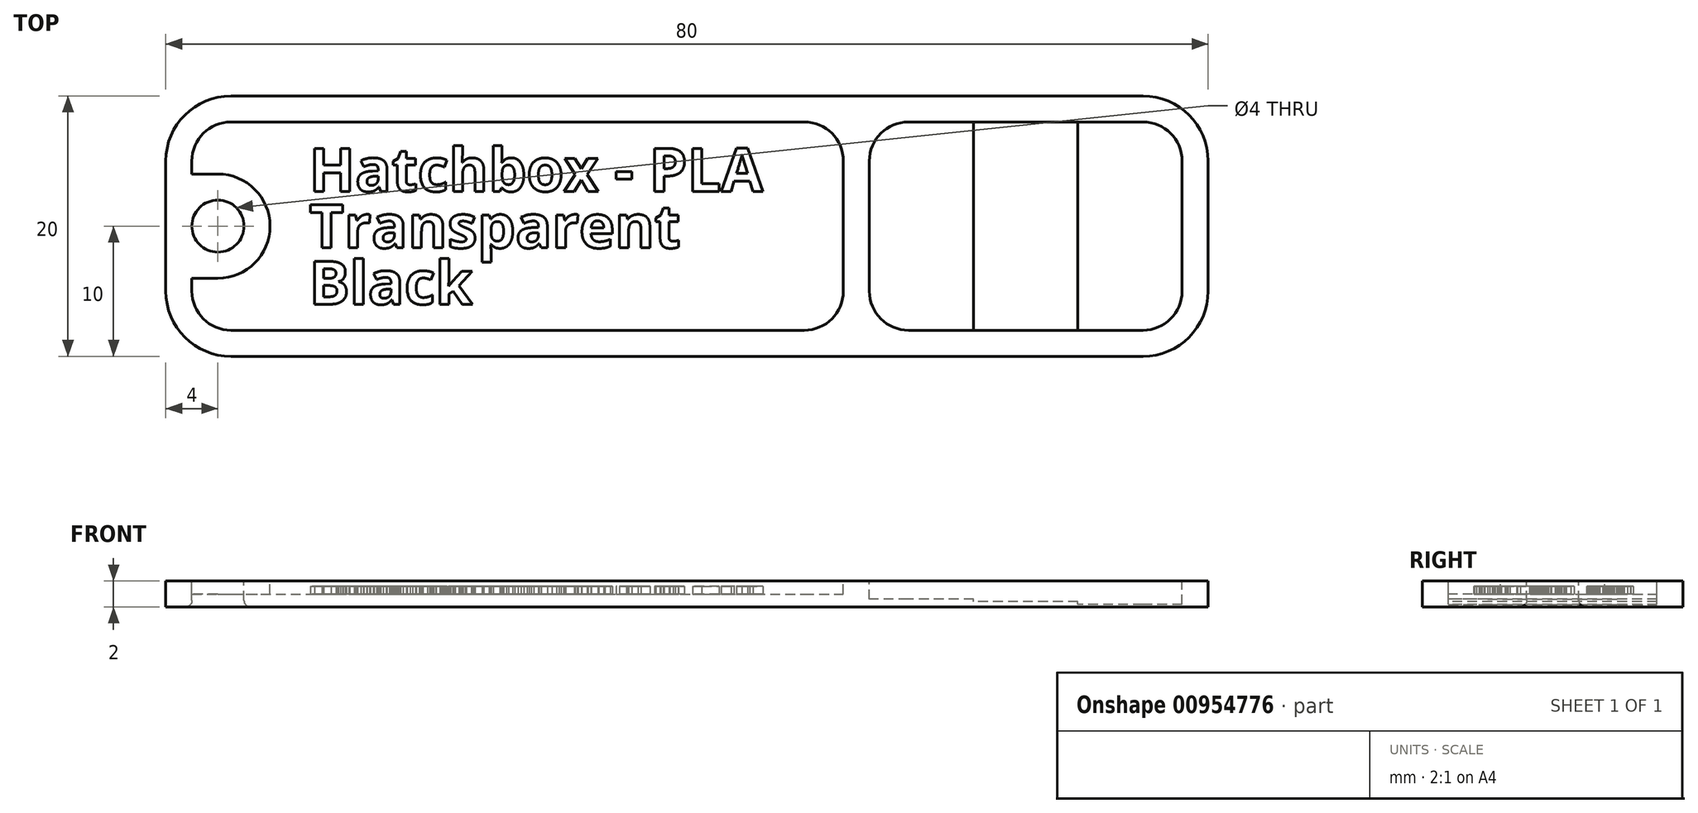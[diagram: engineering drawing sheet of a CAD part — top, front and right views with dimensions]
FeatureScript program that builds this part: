
annotation { "Feature Type Name" : "Feature", "Feature Type Description" : "" }
export const myFeature = defineFeature(function(context is Context, id is Id, definition is map)
    precondition{}
    {
        {
            var Q0;
            Q0=qCreatedBy(makeId("Top.planeOp"),FACE);
            var sketch = newSketch(context, id + "F0", { "sketchPlane" : qUnion([Q0])});
            skLineSegment(sketch, "E0.bottom", {"start": v(35, 10) * mm, "end": v(-35, 10) * mm});
            skLineSegment(sketch, "E0.top", {"start": v(35, -10) * mm, "end": v(-35, -10) * mm});
            skLineSegment(sketch, "E0.left", {"start": v(40, 5) * mm, "end": v(40, -5) * mm});
            skLineSegment(sketch, "E0.right", {"start": v(-40, 5) * mm, "end": v(-40, -5) * mm});
            skPoint(sketch, "E0.middle", {"position": v(0, 0) * mm});
            skPoint(sketch, "E1.visualSharp", {"position": v(-40, 10) * mm});
            skArc(sketch, "E1.filletArc", {"start": v(-35, 10) * mm, "mid": v(-38.54, 8.54) * mm, "end": v(-40, 5) * mm});
            skPoint(sketch, "E2.visualSharp", {"position": v(40, 10) * mm});
            skArc(sketch, "E2.filletArc", {"start": v(40, 5) * mm, "mid": v(38.54, 8.54) * mm, "end": v(35, 10) * mm});
            skPoint(sketch, "E3.visualSharp", {"position": v(40, -10) * mm});
            skArc(sketch, "E3.filletArc", {"start": v(35, -10) * mm, "mid": v(38.54, -8.54) * mm, "end": v(40, -5) * mm});
            skPoint(sketch, "E4.visualSharp", {"position": v(-40, -10) * mm});
            skArc(sketch, "E4.filletArc", {"start": v(-40, -5) * mm, "mid": v(-38.54, -8.54) * mm, "end": v(-35, -10) * mm});
            skSolve(sketch);
        }
        {
            var Q0;
            Q0=qSketchRegion(id+"F0",true);
            extrude(context, id + "F1", {"entities" : qUnion([Q0]), "offsetDistance" : 25 * mm, "depth" : 2 * mm});
        }
        {
            var Q0;
            Q0=makeQuery(id+"F1.opExtrude","CAP_FACE",FACE,{"disambiguationData":[OSD([sQuery(id+"F0.wireOp",EDGE,"E0.bottom"),sQuery(id+"F0.wireOp",EDGE,"E0.top"),sQuery(id+"F0.wireOp",EDGE,"E0.left"),sQuery(id+"F0.wireOp",EDGE,"E0.right"),sQuery(id+"F0.wireOp",EDGE,"E1.filletArc"),sQuery(id+"F0.wireOp",EDGE,"E2.filletArc"),sQuery(id+"F0.wireOp",EDGE,"E3.filletArc"),sQuery(id+"F0.wireOp",EDGE,"E4.filletArc")])],"isStart":false});
            var sketch = newSketch(context, id + "F2", { "sketchPlane" : qUnion([Q0])});
            skLineSegment(sketch, "E5.0", {"start": v(38, -5) * mm, "end": v(38, 5) * mm});
            skArc(sketch, "E5.1", {"start": v(35, -8) * mm, "mid": v(37.12, -7.12) * mm, "end": v(38, -5) * mm});
            skArc(sketch, "E5.2", {"start": v(38, 5) * mm, "mid": v(37.12, 7.12) * mm, "end": v(35, 8) * mm});
            skLineSegment(sketch, "E5.3", {"start": v(-35, -8) * mm, "end": v(9, -8) * mm});
            skLineSegment(sketch, "E5.4", {"start": v(35, 8) * mm, "end": v(17, 8) * mm});
            skArc(sketch, "E5.5", {"start": v(-35, 8) * mm, "mid": v(-37.12, 7.12) * mm, "end": v(-38, 5) * mm});
            skArc(sketch, "E5.7", {"start": v(-38, -5) * mm, "mid": v(-37.12, -7.12) * mm, "end": v(-35, -8) * mm});
            skCircle(sketch, "E6", {"center": v(-36, 0) * mm, "radius": 2 * mm, "construction": true});
            skArc(sketch, "E7.0", {"start": v(-36, -4) * mm, "mid": v(-32, 0) * mm, "end": v(-36, 4) * mm});
            skLineSegment(sketch, "E8", {"start": v(-38, -5) * mm, "end": v(-38, -4) * mm});
            skLineSegment(sketch, "E9", {"start": v(-36, 4) * mm, "end": v(-38, 4) * mm});
            skLineSegment(sketch, "E10", {"start": v(-36, -4) * mm, "end": v(-38, -4) * mm});
            skLineSegment(sketch, "E11.trimOffspring", {"start": v(-38, 4) * mm, "end": v(-38, 5) * mm});
            skArc(sketch, "E12", {"start": v(17, 8) * mm, "mid": v(14.88, 7.12) * mm, "end": v(14, 5) * mm});
            skArc(sketch, "E13", {"start": v(14, -5) * mm, "mid": v(14.88, -7.12) * mm, "end": v(17, -8) * mm});
            skLineSegment(sketch, "E14", {"start": v(14, -5) * mm, "end": v(14, 5) * mm});
            skArc(sketch, "E15", {"start": v(12, 5) * mm, "mid": v(11.12, 7.12) * mm, "end": v(9, 8) * mm});
            skArc(sketch, "E16", {"start": v(12, -5) * mm, "mid": v(11.12, -7.12) * mm, "end": v(9, -8) * mm});
            skLineSegment(sketch, "E17", {"start": v(12, -5) * mm, "end": v(12, 5) * mm});
            skLineSegment(sketch, "E18.trimOffspring", {"start": v(9, 8) * mm, "end": v(-35, 8) * mm});
            skLineSegment(sketch, "E19.trimOffspring", {"start": v(17, -8) * mm, "end": v(35, -8) * mm});
            skSolve(sketch);
        }
        {
            var Q0;
            Q0=qSketchRegion(id+"F2",true);
            extrude(context, id + "F3", {"entities" : qUnion([Q0]), "operationType" : NewBodyOperationType.REMOVE, "oppositeDirection" : true, "offsetDistance" : 25 * mm, "depth" : 1 * mm});
        }
        {
            var Q0;
            Q0=makeQuery(id+"F1.opExtrude","CAP_FACE",FACE,{"disambiguationData":[OSD([sQuery(id+"F0.wireOp",EDGE,"E0.bottom"),sQuery(id+"F0.wireOp",EDGE,"E0.top"),sQuery(id+"F0.wireOp",EDGE,"E0.left"),sQuery(id+"F0.wireOp",EDGE,"E0.right"),sQuery(id+"F0.wireOp",EDGE,"E1.filletArc"),sQuery(id+"F0.wireOp",EDGE,"E2.filletArc"),sQuery(id+"F0.wireOp",EDGE,"E3.filletArc"),sQuery(id+"F0.wireOp",EDGE,"E4.filletArc")])],"isStart":false});
            var sketch = newSketch(context, id + "F4", { "sketchPlane" : qUnion([Q0])});
            skCircle(sketch, "E20.0", {"center": v(-36, 0) * mm, "radius": 2 * mm});
            skSolve(sketch);
        }
        {
            var Q0;
            Q0=qSketchRegion(id+"F4",true);
            extrude(context, id + "F5", {"entities" : qUnion([Q0]), "operationType" : NewBodyOperationType.REMOVE, "endBound" : BoundingType.THROUGH_ALL, "oppositeDirection" : true, "depth" : 25 * mm});
        }
        {
            var Q0;
            Q0=makeQuery(id+"F5.boolean.opBoolean","COPY",EDGE,{"derivedFrom":makeQuery(id+"F5.opExtrude","CAP_EDGE",EDGE,{"disambiguationData":[OSD([sQuery(id+"F4.wireOp",EDGE,"E20.0")])],"isStart":true})});
            var Q1;
            Q1=makeQuery(id+"F5.boolean.opBoolean","INTERSECT",EDGE,{"derivedFrom":[makeQuery(id+"F1.opExtrude","CAP_FACE",FACE,{"disambiguationData":[OSD([sQuery(id+"F0.wireOp",EDGE,"E0.bottom"),sQuery(id+"F0.wireOp",EDGE,"E0.top"),sQuery(id+"F0.wireOp",EDGE,"E0.left"),sQuery(id+"F0.wireOp",EDGE,"E0.right"),sQuery(id+"F0.wireOp",EDGE,"E1.filletArc"),sQuery(id+"F0.wireOp",EDGE,"E2.filletArc"),sQuery(id+"F0.wireOp",EDGE,"E3.filletArc"),sQuery(id+"F0.wireOp",EDGE,"E4.filletArc")])],"isStart":true}),makeQuery(id+"F5.opExtrude","SWEPT_FACE",FACE,{"disambiguationData":[OSD([sQuery(id+"F4.wireOp",EDGE,"E20.0")])]})]});
            fillet(context, id + "F6", {"entities" : qUnion([Q0, Q1]), "radius" : .5 * mm, "tangentPropagation" : true, "allowEdgeOverflow" : false});
        }
        {
            var Q0;
            Q0=makeQuery(id+"F3.boolean.opBoolean","COPY",FACE,{"derivedFrom":makeQuery(id+"F3.opExtrude","CAP_FACE",FACE,{"disambiguationData":[OSD([sQuery(id+"F2.wireOp",EDGE,"E5.0"),sQuery(id+"F2.wireOp",EDGE,"E5.1"),sQuery(id+"F2.wireOp",EDGE,"E5.2"),sQuery(id+"F2.wireOp",EDGE,"E5.4"),sQuery(id+"F2.wireOp",EDGE,"E12"),sQuery(id+"F2.wireOp",EDGE,"E13"),sQuery(id+"F2.wireOp",EDGE,"E14"),sQuery(id+"F2.wireOp",EDGE,"E19.trimOffspring")])],"isStart":false})});
            extrude(context, id + "F7", {"entities" : qUnion([Q0]), "operationType" : NewBodyOperationType.REMOVE, "oppositeDirection" : true, "offsetDistance" : 25 * mm, "depth" : 0.4 * mm});
        }
        {
            var Q0;
            Q0=makeQuery(id+"F7.boolean.opBoolean","COPY",FACE,{"derivedFrom":makeQuery(id+"F7.opExtrude","CAP_FACE",FACE,{"disambiguationData":[OSD([sQuery(id+"F2.wireOp",EDGE,"E5.0"),sQuery(id+"F2.wireOp",EDGE,"E5.1"),sQuery(id+"F2.wireOp",EDGE,"E5.2"),sQuery(id+"F2.wireOp",EDGE,"E5.4"),sQuery(id+"F2.wireOp",EDGE,"E12"),sQuery(id+"F2.wireOp",EDGE,"E13"),sQuery(id+"F2.wireOp",EDGE,"E14"),sQuery(id+"F2.wireOp",EDGE,"E19.trimOffspring")])],"isStart":false})});
            var sketch = newSketch(context, id + "F8", { "sketchPlane" : qUnion([Q0])});
            skArc(sketch, "E21.0.0", {"start": v(35, -8) * mm, "mid": v(37.12, -7.12) * mm, "end": v(38, -5) * mm});
            skLineSegment(sketch, "E21.0.1", {"start": v(38, -5) * mm, "end": v(38, 5) * mm});
            skArc(sketch, "E21.0.2", {"start": v(38, 5) * mm, "mid": v(37.12, 7.12) * mm, "end": v(35, 8) * mm});
            skLineSegment(sketch, "E21.0.3", {"start": v(35, 8) * mm, "end": v(22, 8) * mm});
            skLineSegment(sketch, "E21.0.7", {"start": v(22, -8) * mm, "end": v(35, -8) * mm});
            skLineSegment(sketch, "E22", {"start": v(22, 8) * mm, "end": v(22, -8) * mm});
            skPoint(sketch, "E21.0.4.start.orphan", {"position": v(17, 8) * mm});
            skPoint(sketch, "E21.0.5.start.orphan", {"position": v(14, 5) * mm});
            skPoint(sketch, "E21.0.6.start.orphan", {"position": v(14, -5) * mm});
            skPoint(sketch, "E23.orphan", {"position": v(17, -8) * mm});
            skSolve(sketch);
        }
        {
            var Q0;
            Q0=qSketchRegion(id+"F8",true);
            extrude(context, id + "F9", {"entities" : qUnion([Q0]), "operationType" : NewBodyOperationType.REMOVE, "oppositeDirection" : true, "offsetDistance" : 25 * mm, "depth" : 0.2 * mm});
        }
        {
            var Q0;
            Q0=makeQuery(id+"F9.boolean.opBoolean","COPY",FACE,{"derivedFrom":makeQuery(id+"F9.opExtrude","CAP_FACE",FACE,{"disambiguationData":[OSD([sQuery(id+"F8.wireOp",EDGE,"E21.0.0"),sQuery(id+"F8.wireOp",EDGE,"E21.0.1"),sQuery(id+"F8.wireOp",EDGE,"E21.0.2"),sQuery(id+"F8.wireOp",EDGE,"E21.0.3"),sQuery(id+"F8.wireOp",EDGE,"E21.0.7"),sQuery(id+"F8.wireOp",EDGE,"E22")])],"isStart":false})});
            var sketch = newSketch(context, id + "F10", { "sketchPlane" : qUnion([Q0])});
            skLineSegment(sketch, "E24.0.0", {"start": v(35, 8) * mm, "end": v(30, 8) * mm});
            skLineSegment(sketch, "E24.0.2", {"start": v(30, -8) * mm, "end": v(35, -8) * mm});
            skArc(sketch, "E24.0.3", {"start": v(35, -8) * mm, "mid": v(37.12, -7.12) * mm, "end": v(38, -5) * mm});
            skLineSegment(sketch, "E24.0.4", {"start": v(38, -5) * mm, "end": v(38, 5) * mm});
            skArc(sketch, "E24.0.5", {"start": v(38, 5) * mm, "mid": v(37.12, 7.12) * mm, "end": v(35, 8) * mm});
            skLineSegment(sketch, "E25", {"start": v(30, 8) * mm, "end": v(30, -8) * mm});
            skPoint(sketch, "E24.0.1.end.orphan", {"position": v(22, -8) * mm});
            skPoint(sketch, "E26.orphan", {"position": v(22, 8) * mm});
            skSolve(sketch);
        }
        {
            var Q0;
            Q0=makeQuery(id+"F10.imprint","IMPRINT",FACE,{"disambiguationData":[TD([[makeQuery(id+"F10.imprint","IMPRINT",EDGE,{"derivedFrom":sQuery(id+"F10.wireOp",EDGE,"E24.0.0")}),1.0]])]});
            extrude(context, id + "F11", {"entities" : qUnion([Q0]), "operationType" : NewBodyOperationType.REMOVE, "oppositeDirection" : true, "offsetDistance" : 25 * mm, "depth" : 0.2 * mm});
        }
        {
            var Q0;
            Q0=makeQuery(id+"F3.boolean.opBoolean","COPY",FACE,{"derivedFrom":makeQuery(id+"F3.opExtrude","CAP_FACE",FACE,{"disambiguationData":[OSD([sQuery(id+"F2.wireOp",EDGE,"E5.3"),sQuery(id+"F2.wireOp",EDGE,"E5.5"),sQuery(id+"F2.wireOp",EDGE,"E5.7"),sQuery(id+"F2.wireOp",EDGE,"E7.0"),sQuery(id+"F2.wireOp",EDGE,"E8"),sQuery(id+"F2.wireOp",EDGE,"E9"),sQuery(id+"F2.wireOp",EDGE,"E10"),sQuery(id+"F2.wireOp",EDGE,"E11.trimOffspring"),sQuery(id+"F2.wireOp",EDGE,"E15"),sQuery(id+"F2.wireOp",EDGE,"E16"),sQuery(id+"F2.wireOp",EDGE,"E17"),sQuery(id+"F2.wireOp",EDGE,"E18.trimOffspring")])],"isStart":false})});
            var sketch = newSketch(context, id + "F12", { "sketchPlane" : qUnion([Q0])});
            skText(sketch, "E27", { "text": "Hatchbox - PLA", "fontName": "OpenSans-Bold.ttf"});
            skText(sketch, "E28", { "text": "Transparent", "fontName": "OpenSans-Bold.ttf"});
            skText(sketch, "E29", { "text": "Black", "fontName": "OpenSans-Bold.ttf"});
            skLineSegment(sketch, "E30", {"start": v(-27.83, 1.67) * mm, "end": v(-27.83, 2.67) * mm, "construction": true});
            skLineSegment(sketch, "E31", {"start": v(-26.66, -2.67) * mm, "end": v(-26.66, -1.67) * mm, "construction": true});
            skLineSegment(sketch, "E32.bottom", {"start": v(-31, 7) * mm, "end": v(10, 7) * mm, "construction": true});
            skLineSegment(sketch, "E32.top", {"start": v(-31, -7) * mm, "end": v(10, -7) * mm, "construction": true});
            skLineSegment(sketch, "E32.left", {"start": v(-31, 7) * mm, "end": v(-31, -7) * mm, "construction": true});
            skLineSegment(sketch, "E32.right", {"start": v(10, 7) * mm, "end": v(10, -7) * mm, "construction": true});
            skLineSegment(sketch, "E33", {"start": v(-13.47, 7) * mm, "end": v(-13.47, 8) * mm, "construction": true});
            skLineSegment(sketch, "E34", {"start": v(-13.67, -7) * mm, "end": v(-13.67, -8) * mm, "construction": true});
            skLineSegment(sketch, "E35", {"start": v(-32, 0) * mm, "end": v(-31, 0) * mm, "construction": true});
            skPoint(sketch, "E35.startSnap0", {"position": v(-31, 0) * mm});
            skLineSegment(sketch, "E36", {"start": v(-29, 4.33) * mm, "end": v(-31, 4.33) * mm, "construction": true});
            skLineSegment(sketch, "E37", {"start": v(10, 1.23) * mm, "end": v(12, 1.23) * mm, "construction": true});
            skLineSegment(sketch, "E38", {"start": v(-29, -0.54) * mm, "end": v(-31, -0.54) * mm, "construction": true});
            skLineSegment(sketch, "E39", {"start": v(-29, -4.33) * mm, "end": v(-31, -4.33) * mm, "construction": true});
            skLineSegment(sketch, "E40", {"start": v(-25.76, 6) * mm, "end": v(-25.76, 7) * mm, "construction": true});
            skLineSegment(sketch, "E41", {"start": v(-26.93, -6) * mm, "end": v(-26.93, -7) * mm, "construction": true});
            const initialGuessF12  = {"E27": [-0.029, 0.00267, 1, 0, 0.00333], "E28": [-0.029, -0.00167, 1, 0, 0.00333], "E29": [-0.029, -0.006, 1, 0, 0.00333]};
            skSetInitialGuess(sketch, initialGuessF12);
            skSolve(sketch);
        }
        {
            var Q0;
            Q0=qSketchRegion(id+"F12",true);
            extrude(context, id + "F13", {"entities" : qUnion([Q0]), "operationType" : NewBodyOperationType.ADD, "depth" : 0.6 * mm, "offsetDistance" : 25 * mm});
        }
    });
